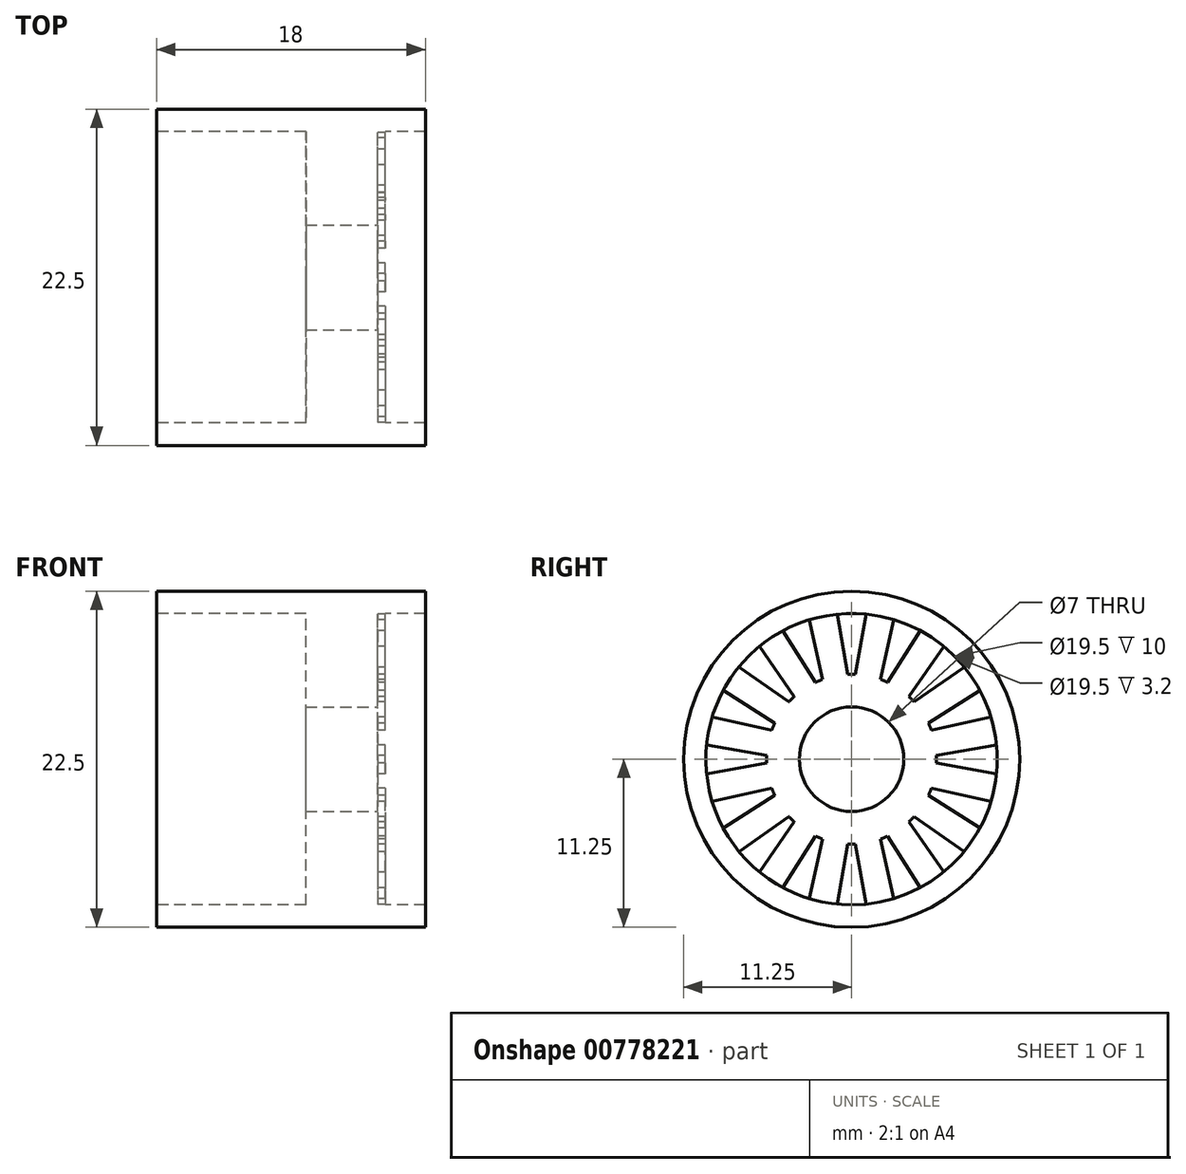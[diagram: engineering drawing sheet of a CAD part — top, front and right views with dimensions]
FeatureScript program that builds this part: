
annotation { "Feature Type Name" : "Feature", "Feature Type Description" : "" }
export const myFeature = defineFeature(function(context is Context, id is Id, definition is map)
    precondition{}
    {
        {
            var Q0;
            Q0=qCreatedBy(makeId("Right.planeOp"),FACE);
            var sketch = newSketch(context, id + "F0", { "sketchPlane" : qUnion([Q0])});
            skCircle(sketch, "E0", {"center": v(0, 0) * mm, "radius": 9.75 * mm});
            skSolve(sketch);
        }
        {
            var Q0;
            Q0=makeQuery(id+"F0.imprint","IMPRINT",FACE,{"disambiguationData":[TD([[makeQuery(id+"F0.imprint","IMPRINT",EDGE,{"derivedFrom":sQuery(id+"F0.wireOp",EDGE,"E0")}),1.0]])]});
            var sketch = newSketch(context, id + "F1", { "sketchPlane" : qUnion([Q0])});
            skCircle(sketch, "E1", {"center": v(0, 0) * mm, "radius": 11.25 * mm});
            skSolve(sketch);
        }
        {
            var Q0;
            Q0=makeQuery(id+"F0.imprint","IMPRINT",FACE,{"disambiguationData":[TD([[makeQuery(id+"F0.imprint","IMPRINT",EDGE,{"derivedFrom":sQuery(id+"F0.wireOp",EDGE,"E0")}),1.0]])]});
            extrude(context, id + "F2", {"entities" : qUnion([Q0]), "depth" : 18 * mm, "offsetDistance" : 25 * mm});
        }
        {
            var Q0;
            Q0=makeQuery(id+"F1.imprint","IMPRINT",FACE,{"disambiguationData":[TD([[makeQuery(id+"F1.imprint","IMPRINT",EDGE,{"derivedFrom":sQuery(id+"F1.wireOp",EDGE,"E1")}),1.0]])]});
            extrude(context, id + "F3", {"entities" : qUnion([Q0]), "depth" : 18 * mm, "offsetDistance" : 25 * mm});
        }
        {
            var Q0;
            Q0=makeQuery(id+"F2.opExtrude","CAP_FACE",FACE,{"disambiguationData":[OSD([sQuery(id+"F0.wireOp",EDGE,"E0")])],"isStart":true});
            extrude(context, id + "F4", {"entities" : qUnion([Q0]), "operationType" : NewBodyOperationType.REMOVE, "oppositeDirection" : true, "depth" : 10 * mm, "offsetDistance" : 25 * mm});
        }
        {
            var Q0;
            Q0=makeQuery(id+"F2.opExtrude","CAP_FACE",FACE,{"disambiguationData":[OSD([sQuery(id+"F0.wireOp",EDGE,"E0")])],"isStart":false});
            extrude(context, id + "F5", {"entities" : qUnion([Q0]), "operationType" : NewBodyOperationType.REMOVE, "oppositeDirection" : true, "depth" : 3.2 * mm, "offsetDistance" : 25 * mm});
        }
        {
            var Q0;
            Q0=makeQuery(id+"F5.boolean.opBoolean","COPY",FACE,{"derivedFrom":makeQuery(id+"F5.opExtrude","CAP_FACE",FACE,{"disambiguationData":[OSD([sQuery(id+"F0.wireOp",EDGE,"E0")])],"isStart":false})});
            var sketch = newSketch(context, id + "F6", { "sketchPlane" : qUnion([Q0])});
            skCircle(sketch, "E2", {"center": v(0, 0) * mm, "radius": 3.5 * mm});
            skSolve(sketch);
        }
        {
            var Q0;
            Q0=makeQuery(id+"F6.imprint","IMPRINT",FACE,{"disambiguationData":[TD([[makeQuery(id+"F6.imprint","IMPRINT",EDGE,{"derivedFrom":sQuery(id+"F6.wireOp",EDGE,"E2")}),1.0]])]});
            extrude(context, id + "F7", {"entities" : qUnion([Q0]), "operationType" : NewBodyOperationType.REMOVE, "endBound" : BoundingType.THROUGH_ALL, "oppositeDirection" : true, "depth" : 25 * mm, "offsetDistance" : 25 * mm});
        }
        {
            var Q0;
            Q0=makeQuery(id+"F5.boolean.opBoolean","COPY",FACE,{"derivedFrom":makeQuery(id+"F5.opExtrude","CAP_FACE",FACE,{"disambiguationData":[OSD([sQuery(id+"F0.wireOp",EDGE,"E0")])],"isStart":false})});
            var sketch = newSketch(context, id + "F8", { "sketchPlane" : qUnion([Q0])});
            skCircle(sketch, "E3", {"center": v(0, 0) * mm, "radius": 4.22 * mm, "construction": true});
            skLineSegment(sketch, "E4", {"start": v(0, 4.22) * mm, "end": v(0.97, 9.7) * mm});
            skLineSegment(sketch, "E5", {"start": v(0, 0) * mm, "end": v(0, 9.75) * mm, "construction": true});
            skLineSegment(sketch, "E6.MirrorCS", {"start": v(0, 4.22) * mm, "end": v(-0.97, 9.7) * mm});
            skCircle(sketch, "E7", {"center": v(0, 0) * mm, "radius": 9.75 * mm});
            skLineSegment(sketch, "E8.1.0", {"start": v(-2.98, 2.98) * mm, "end": v(-6.18, 7.54) * mm});
            skLineSegment(sketch, "E8.1.1", {"start": v(-2.98, 2.98) * mm, "end": v(-7.54, 6.18) * mm});
            skLineSegment(sketch, "E8.2.0", {"start": v(-4.22, 0) * mm, "end": v(-9.7, 0.97) * mm});
            skLineSegment(sketch, "E8.2.1", {"start": v(-4.22, 0) * mm, "end": v(-9.7, -0.97) * mm});
            skLineSegment(sketch, "E8.3.0", {"start": v(-2.98, -2.98) * mm, "end": v(-7.54, -6.18) * mm});
            skLineSegment(sketch, "E8.3.1", {"start": v(-2.98, -2.98) * mm, "end": v(-6.18, -7.54) * mm});
            skLineSegment(sketch, "E8.4.0", {"start": v(0, -4.22) * mm, "end": v(-0.97, -9.7) * mm});
            skLineSegment(sketch, "E8.4.1", {"start": v(0, -4.22) * mm, "end": v(0.97, -9.7) * mm});
            skLineSegment(sketch, "E8.5.0", {"start": v(2.98, -2.98) * mm, "end": v(6.18, -7.54) * mm});
            skLineSegment(sketch, "E8.5.1", {"start": v(2.98, -2.98) * mm, "end": v(7.54, -6.18) * mm});
            skLineSegment(sketch, "E8.6.0", {"start": v(4.22, 0) * mm, "end": v(9.7, -0.97) * mm});
            skLineSegment(sketch, "E8.6.1", {"start": v(4.22, 0) * mm, "end": v(9.7, 0.97) * mm});
            skLineSegment(sketch, "E8.7.0", {"start": v(2.98, 2.98) * mm, "end": v(7.54, 6.18) * mm});
            skLineSegment(sketch, "E8.7.1", {"start": v(2.98, 2.98) * mm, "end": v(6.18, 7.54) * mm});
            skLineSegment(sketch, "E9", {"start": v(0, 0) * mm, "end": v(3.73, 9) * mm, "construction": true});
            skLineSegment(sketch, "E10", {"start": v(1.61, 3.9) * mm, "end": v(4.6, 8.6) * mm});
            skLineSegment(sketch, "E11.MirrorCS", {"start": v(1.61, 3.9) * mm, "end": v(2.82, 9.33) * mm});
            skLineSegment(sketch, "E12.1.0", {"start": v(-1.61, 3.9) * mm, "end": v(-2.82, 9.33) * mm});
            skLineSegment(sketch, "E12.1.1", {"start": v(-1.61, 3.9) * mm, "end": v(-4.6, 8.6) * mm});
            skLineSegment(sketch, "E12.2.0", {"start": v(-3.9, 1.61) * mm, "end": v(-8.6, 4.6) * mm});
            skLineSegment(sketch, "E12.2.1", {"start": v(-3.9, 1.61) * mm, "end": v(-9.33, 2.82) * mm});
            skLineSegment(sketch, "E12.3.0", {"start": v(-3.9, -1.61) * mm, "end": v(-9.33, -2.82) * mm});
            skLineSegment(sketch, "E12.3.1", {"start": v(-3.9, -1.61) * mm, "end": v(-8.6, -4.6) * mm});
            skLineSegment(sketch, "E12.4.0", {"start": v(-1.61, -3.9) * mm, "end": v(-4.6, -8.6) * mm});
            skLineSegment(sketch, "E12.4.1", {"start": v(-1.61, -3.9) * mm, "end": v(-2.82, -9.33) * mm});
            skLineSegment(sketch, "E12.5.0", {"start": v(1.61, -3.9) * mm, "end": v(2.82, -9.33) * mm});
            skLineSegment(sketch, "E12.5.1", {"start": v(1.61, -3.9) * mm, "end": v(4.6, -8.6) * mm});
            skLineSegment(sketch, "E12.6.0", {"start": v(3.9, -1.61) * mm, "end": v(8.6, -4.6) * mm});
            skLineSegment(sketch, "E12.6.1", {"start": v(3.9, -1.61) * mm, "end": v(9.33, -2.82) * mm});
            skLineSegment(sketch, "E12.7.0", {"start": v(3.9, 1.61) * mm, "end": v(9.33, 2.82) * mm});
            skLineSegment(sketch, "E12.7.1", {"start": v(3.9, 1.61) * mm, "end": v(8.6, 4.6) * mm});
            skCircle(sketch, "E13", {"center": v(0, 0) * mm, "radius": 5.68 * mm});
            skSolve(sketch);
        }
        {
            var Q0;
            {var subQ0=sQuery(id+"F8.wireOp",EDGE,"E8.1.0");var subQ1=sQuery(id+"F8.wireOp",EDGE,"E7");var subQ2=makeQuery(id+"F8.imprint","INTERSECT",VERTEX,{"derivedFrom":[subQ1,subQ0]});Q0=makeQuery(id+"F8.imprint","IMPRINT",FACE,{"disambiguationData":[TD([[makeQuery(id+"F8.imprint","IMPRINT",EDGE,{"disambiguationData":[TD([[subQ2,-1.0]])],"derivedFrom":subQ1}),1.0]])]});}
            var Q1;
            {var subQ0=sQuery(id+"F8.wireOp",EDGE,"E12.1.0");var subQ1=sQuery(id+"F8.wireOp",EDGE,"E7");var subQ2=makeQuery(id+"F8.imprint","INTERSECT",VERTEX,{"derivedFrom":[subQ1,subQ0]});Q1=makeQuery(id+"F8.imprint","IMPRINT",FACE,{"disambiguationData":[TD([[makeQuery(id+"F8.imprint","IMPRINT",EDGE,{"disambiguationData":[TD([[subQ2,-1.0]])],"derivedFrom":subQ1}),1.0]])]});}
            var Q2;
            {var subQ0=sQuery(id+"F8.wireOp",EDGE,"E7");var subQ1=sQuery(id+"F8.wireOp",EDGE,"E4");var subQ2=makeQuery(id+"F8.imprint","INTERSECT",VERTEX,{"derivedFrom":[subQ1,subQ0]});Q2=makeQuery(id+"F8.imprint","IMPRINT",FACE,{"disambiguationData":[TD([[makeQuery(id+"F8.imprint","IMPRINT",EDGE,{"disambiguationData":[TD([[subQ2,1.0]])],"derivedFrom":subQ1}),1.0]])]});}
            var Q3;
            {var subQ0=sQuery(id+"F8.wireOp",EDGE,"E10");var subQ1=sQuery(id+"F8.wireOp",EDGE,"E7");var subQ2=makeQuery(id+"F8.imprint","INTERSECT",VERTEX,{"derivedFrom":[subQ1,subQ0]});Q3=makeQuery(id+"F8.imprint","IMPRINT",FACE,{"disambiguationData":[TD([[makeQuery(id+"F8.imprint","IMPRINT",EDGE,{"disambiguationData":[TD([[subQ2,-1.0]])],"derivedFrom":subQ1}),1.0]])]});}
            var Q4;
            {var subQ0=sQuery(id+"F8.wireOp",EDGE,"E8.7.0");var subQ1=sQuery(id+"F8.wireOp",EDGE,"E7");var subQ2=makeQuery(id+"F8.imprint","INTERSECT",VERTEX,{"derivedFrom":[subQ1,subQ0]});Q4=makeQuery(id+"F8.imprint","IMPRINT",FACE,{"disambiguationData":[TD([[makeQuery(id+"F8.imprint","IMPRINT",EDGE,{"disambiguationData":[TD([[subQ2,-1.0]])],"derivedFrom":subQ1}),1.0]])]});}
            var Q5;
            {var subQ0=sQuery(id+"F8.wireOp",EDGE,"E12.7.0");var subQ1=sQuery(id+"F8.wireOp",EDGE,"E7");var subQ2=makeQuery(id+"F8.imprint","INTERSECT",VERTEX,{"derivedFrom":[subQ1,subQ0]});Q5=makeQuery(id+"F8.imprint","IMPRINT",FACE,{"disambiguationData":[TD([[makeQuery(id+"F8.imprint","IMPRINT",EDGE,{"disambiguationData":[TD([[subQ2,-1.0]])],"derivedFrom":subQ1}),1.0]])]});}
            var Q6;
            {var subQ0=sQuery(id+"F8.wireOp",EDGE,"E8.6.0");var subQ1=sQuery(id+"F8.wireOp",EDGE,"E7");var subQ2=makeQuery(id+"F8.imprint","INTERSECT",VERTEX,{"derivedFrom":[subQ1,subQ0]});Q6=makeQuery(id+"F8.imprint","IMPRINT",FACE,{"disambiguationData":[TD([[makeQuery(id+"F8.imprint","IMPRINT",EDGE,{"disambiguationData":[TD([[subQ2,-1.0]])],"derivedFrom":subQ1}),1.0]])]});}
            var Q7;
            {var subQ0=sQuery(id+"F8.wireOp",EDGE,"E12.6.0");var subQ1=sQuery(id+"F8.wireOp",EDGE,"E7");var subQ2=makeQuery(id+"F8.imprint","INTERSECT",VERTEX,{"derivedFrom":[subQ1,subQ0]});Q7=makeQuery(id+"F8.imprint","IMPRINT",FACE,{"disambiguationData":[TD([[makeQuery(id+"F8.imprint","IMPRINT",EDGE,{"disambiguationData":[TD([[subQ2,-1.0]])],"derivedFrom":subQ1}),1.0]])]});}
            var Q8;
            {var subQ0=sQuery(id+"F8.wireOp",EDGE,"E8.5.0");var subQ1=sQuery(id+"F8.wireOp",EDGE,"E7");var subQ2=makeQuery(id+"F8.imprint","INTERSECT",VERTEX,{"derivedFrom":[subQ1,subQ0]});Q8=makeQuery(id+"F8.imprint","IMPRINT",FACE,{"disambiguationData":[TD([[makeQuery(id+"F8.imprint","IMPRINT",EDGE,{"disambiguationData":[TD([[subQ2,-1.0]])],"derivedFrom":subQ1}),1.0]])]});}
            var Q9;
            {var subQ0=sQuery(id+"F8.wireOp",EDGE,"E12.5.0");var subQ1=sQuery(id+"F8.wireOp",EDGE,"E7");var subQ2=makeQuery(id+"F8.imprint","INTERSECT",VERTEX,{"derivedFrom":[subQ1,subQ0]});Q9=makeQuery(id+"F8.imprint","IMPRINT",FACE,{"disambiguationData":[TD([[makeQuery(id+"F8.imprint","IMPRINT",EDGE,{"disambiguationData":[TD([[subQ2,-1.0]])],"derivedFrom":subQ1}),1.0]])]});}
            var Q10;
            {var subQ0=sQuery(id+"F8.wireOp",EDGE,"E8.4.0");var subQ1=sQuery(id+"F8.wireOp",EDGE,"E7");var subQ2=makeQuery(id+"F8.imprint","INTERSECT",VERTEX,{"derivedFrom":[subQ1,subQ0]});Q10=makeQuery(id+"F8.imprint","IMPRINT",FACE,{"disambiguationData":[TD([[makeQuery(id+"F8.imprint","IMPRINT",EDGE,{"disambiguationData":[TD([[subQ2,-1.0]])],"derivedFrom":subQ1}),1.0]])]});}
            var Q11;
            {var subQ0=sQuery(id+"F8.wireOp",EDGE,"E12.4.0");var subQ1=sQuery(id+"F8.wireOp",EDGE,"E7");var subQ2=makeQuery(id+"F8.imprint","INTERSECT",VERTEX,{"derivedFrom":[subQ1,subQ0]});Q11=makeQuery(id+"F8.imprint","IMPRINT",FACE,{"disambiguationData":[TD([[makeQuery(id+"F8.imprint","IMPRINT",EDGE,{"disambiguationData":[TD([[subQ2,-1.0]])],"derivedFrom":subQ1}),1.0]])]});}
            var Q12;
            {var subQ0=sQuery(id+"F8.wireOp",EDGE,"E8.3.0");var subQ1=sQuery(id+"F8.wireOp",EDGE,"E7");var subQ2=makeQuery(id+"F8.imprint","INTERSECT",VERTEX,{"derivedFrom":[subQ1,subQ0]});Q12=makeQuery(id+"F8.imprint","IMPRINT",FACE,{"disambiguationData":[TD([[makeQuery(id+"F8.imprint","IMPRINT",EDGE,{"disambiguationData":[TD([[subQ2,-1.0]])],"derivedFrom":subQ1}),1.0]])]});}
            var Q13;
            {var subQ0=sQuery(id+"F8.wireOp",EDGE,"E12.3.0");var subQ1=sQuery(id+"F8.wireOp",EDGE,"E7");var subQ2=makeQuery(id+"F8.imprint","INTERSECT",VERTEX,{"derivedFrom":[subQ1,subQ0]});Q13=makeQuery(id+"F8.imprint","IMPRINT",FACE,{"disambiguationData":[TD([[makeQuery(id+"F8.imprint","IMPRINT",EDGE,{"disambiguationData":[TD([[subQ2,-1.0]])],"derivedFrom":subQ1}),1.0]])]});}
            var Q14;
            {var subQ0=sQuery(id+"F8.wireOp",EDGE,"E8.2.0");var subQ1=sQuery(id+"F8.wireOp",EDGE,"E7");var subQ2=makeQuery(id+"F8.imprint","INTERSECT",VERTEX,{"derivedFrom":[subQ1,subQ0]});Q14=makeQuery(id+"F8.imprint","IMPRINT",FACE,{"disambiguationData":[TD([[makeQuery(id+"F8.imprint","IMPRINT",EDGE,{"disambiguationData":[TD([[subQ2,-1.0]])],"derivedFrom":subQ1}),1.0]])]});}
            var Q15;
            {var subQ0=sQuery(id+"F8.wireOp",EDGE,"E12.2.0");var subQ1=sQuery(id+"F8.wireOp",EDGE,"E7");var subQ2=makeQuery(id+"F8.imprint","INTERSECT",VERTEX,{"derivedFrom":[subQ1,subQ0]});Q15=makeQuery(id+"F8.imprint","IMPRINT",FACE,{"disambiguationData":[TD([[makeQuery(id+"F8.imprint","IMPRINT",EDGE,{"disambiguationData":[TD([[subQ2,-1.0]])],"derivedFrom":subQ1}),1.0]])]});}
            extrude(context, id + "F9", {"entities" : qUnion([Q0, Q1, Q2, Q3, Q4, Q5, Q6, Q7, Q8, Q9, Q10, Q11, Q12, Q13, Q14, Q15]), "operationType" : NewBodyOperationType.ADD, "depth" : .5 * mm, "offsetDistance" : 25 * mm});
        }
    });
